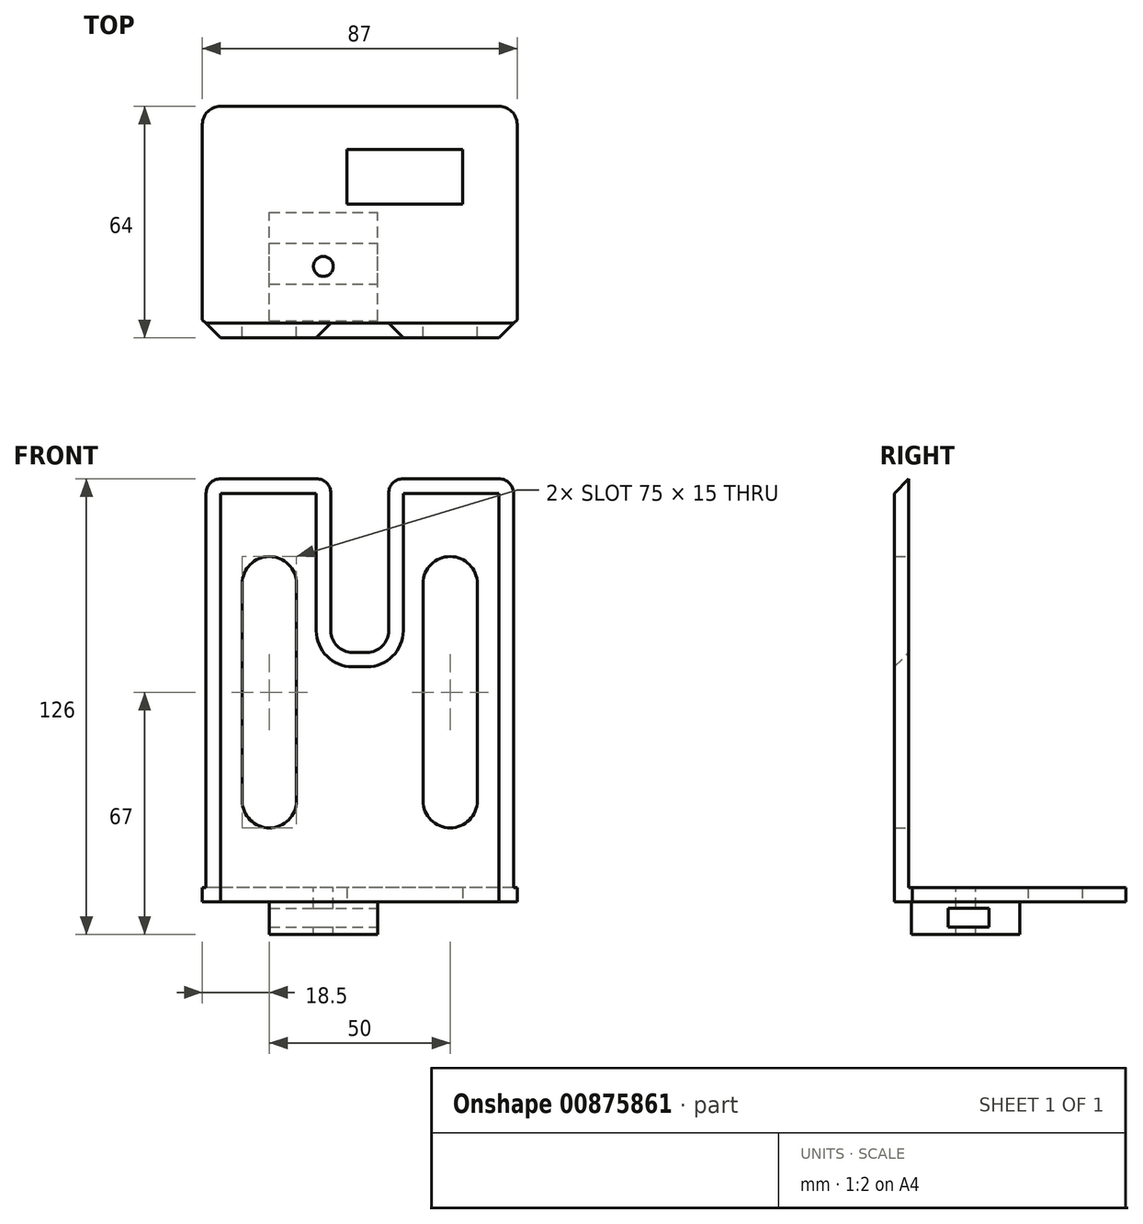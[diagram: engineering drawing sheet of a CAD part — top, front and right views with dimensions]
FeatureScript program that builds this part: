
annotation { "Feature Type Name" : "Feature", "Feature Type Description" : "" }
export const myFeature = defineFeature(function(context is Context, id is Id, definition is map)
    precondition{}
    {
        {
            var Q0;
            Q0=qCreatedBy(makeId("Front.planeOp"),FACE);
            var sketch = newSketch(context, id + "F0", { "sketchPlane" : qUnion([Q0])});
            skLineSegment(sketch, "E0.bottom", {"start": v(-43.5, 78.39) * mm, "end": v(43.5, 78.39) * mm});
            skLineSegment(sketch, "E0.top", {"start": v(-43.5, -39.61) * mm, "end": v(43.5, -39.61) * mm});
            skLineSegment(sketch, "E0.left", {"start": v(-43.5, 78.39) * mm, "end": v(-43.5, -39.61) * mm});
            skLineSegment(sketch, "E0.right", {"start": v(43.5, 78.39) * mm, "end": v(43.5, -39.61) * mm});
            skLineSegment(sketch, "E1", {"start": v(25, -11.61) * mm, "end": v(25, 48.39) * mm});
            skLineSegment(sketch, "E2.MirrorCS", {"start": v(-25, -11.61) * mm, "end": v(-25, 48.39) * mm});
            skArc(sketch, "E3.0.startCap", {"start": v(-17.5, -11.61) * mm, "mid": v(-25, -19.11) * mm, "end": v(-32.5, -11.61) * mm});
            skArc(sketch, "E3.0.endCap", {"start": v(-32.5, 48.39) * mm, "mid": v(-25, 55.89) * mm, "end": v(-17.5, 48.39) * mm});
            skLineSegment(sketch, "E3.0.left", {"start": v(-32.5, -11.61) * mm, "end": v(-32.5, 48.39) * mm});
            skLineSegment(sketch, "E3.0.right", {"start": v(-17.5, -11.61) * mm, "end": v(-17.5, 48.39) * mm});
            skLineSegment(sketch, "E4.bottom", {"start": v(-7, 78.39) * mm, "end": v(7, 78.39) * mm});
            skLineSegment(sketch, "E4.top", {"start": v(-7, 30.39) * mm, "end": v(7, 30.39) * mm});
            skLineSegment(sketch, "E4.left", {"start": v(-7, 78.39) * mm, "end": v(-7, 30.39) * mm});
            skLineSegment(sketch, "E4.right", {"start": v(7, 78.39) * mm, "end": v(7, 30.39) * mm});
            skArc(sketch, "E5.0.startCap", {"start": v(32.5, -11.61) * mm, "mid": v(25, -19.11) * mm, "end": v(17.5, -11.61) * mm});
            skArc(sketch, "E5.0.endCap", {"start": v(17.5, 48.39) * mm, "mid": v(25, 55.89) * mm, "end": v(32.5, 48.39) * mm});
            skLineSegment(sketch, "E5.0.left", {"start": v(17.5, -11.61) * mm, "end": v(17.5, 48.39) * mm});
            skLineSegment(sketch, "E5.0.right", {"start": v(32.5, -11.61) * mm, "end": v(32.5, 48.39) * mm});
            skSolve(sketch);
        }
        {
            var Q0;
            Q0=makeQuery(id+"F0.imprint","IMPRINT",FACE,{"disambiguationData":[TD([[makeQuery(id+"F0.imprint","IMPRINT",EDGE,{"derivedFrom":sQuery(id+"F0.wireOp",EDGE,"E0.top")}),1.0]])]});
            extrude(context, id + "F1", {"entities" : qUnion([Q0]), "depth" : 4 * mm, "offsetDistance" : 25 * mm});
        }
        {
            var Q0;
            Q0=makeQuery(id+"F1.opExtrude","CAP_FACE",FACE,{"disambiguationData":[OSD([sQuery(id+"F0.wireOp",EDGE,"E0.bottom"),sQuery(id+"F0.wireOp",EDGE,"E0.top"),sQuery(id+"F0.wireOp",EDGE,"E0.left"),sQuery(id+"F0.wireOp",EDGE,"E0.right"),sQuery(id+"F0.wireOp",EDGE,"E3.0.startCap"),sQuery(id+"F0.wireOp",EDGE,"E3.0.endCap"),sQuery(id+"F0.wireOp",EDGE,"E3.0.left"),sQuery(id+"F0.wireOp",EDGE,"E3.0.right"),sQuery(id+"F0.wireOp",EDGE,"E4.top"),sQuery(id+"F0.wireOp",EDGE,"E4.left"),sQuery(id+"F0.wireOp",EDGE,"E4.right"),sQuery(id+"F0.wireOp",EDGE,"E5.0.startCap"),sQuery(id+"F0.wireOp",EDGE,"E5.0.endCap"),sQuery(id+"F0.wireOp",EDGE,"E5.0.left"),sQuery(id+"F0.wireOp",EDGE,"E5.0.right")])],"isStart":true});
            var sketch = newSketch(context, id + "F2", { "sketchPlane" : qUnion([Q0])});
            skLineSegment(sketch, "E6.bottom", {"start": v(-43.5, -35.61) * mm, "end": v(43.5, -35.61) * mm});
            skLineSegment(sketch, "E6.top", {"start": v(-43.5, -39.61) * mm, "end": v(43.5, -39.61) * mm});
            skLineSegment(sketch, "E6.left", {"start": v(-43.5, -35.61) * mm, "end": v(-43.5, -39.61) * mm});
            skLineSegment(sketch, "E6.right", {"start": v(43.5, -35.61) * mm, "end": v(43.5, -39.61) * mm});
            skSolve(sketch);
        }
        {
            var Q0;
            Q0=makeQuery(id+"F2.imprint","IMPRINT",FACE,{"disambiguationData":[TD([[makeQuery(id+"F2.imprint","IMPRINT",EDGE,{"derivedFrom":sQuery(id+"F2.wireOp",EDGE,"E6.bottom")}),-1.0]])]});
            extrude(context, id + "F3", {"entities" : qUnion([Q0]), "operationType" : NewBodyOperationType.ADD, "depth" : 60 * mm, "offsetDistance" : 25 * mm});
        }
        {
            var Q0;
            Q0=makeQuery(id+"F3.boolean.opBoolean","MERGE",FACE,{"derivedFrom":[makeQuery(id+"F1.opExtrude","SWEPT_FACE",FACE,{"disambiguationData":[OSD([sQuery(id+"F0.wireOp",EDGE,"E0.top")])]}),makeQuery(id+"F3.opExtrude","SWEPT_FACE",FACE,{"disambiguationData":[OSD([sQuery(id+"F2.wireOp",EDGE,"E6.top")])]})]});
            var sketch = newSketch(context, id + "F4", { "sketchPlane" : qUnion([Q0])});
            skLineSegment(sketch, "E7.bottom", {"start": v(28.5, -33) * mm, "end": v(-3.5, -33) * mm});
            skLineSegment(sketch, "E7.top", {"start": v(28.5, -48) * mm, "end": v(-3.5, -48) * mm});
            skLineSegment(sketch, "E7.left", {"start": v(28.5, -33) * mm, "end": v(28.5, -48) * mm});
            skLineSegment(sketch, "E7.right", {"start": v(-3.5, -33) * mm, "end": v(-3.5, -48) * mm});
            skSolve(sketch);
        }
        {
            var Q0;
            Q0=makeQuery(id+"F4.imprint","IMPRINT",FACE,{"disambiguationData":[TD([[makeQuery(id+"F4.imprint","IMPRINT",EDGE,{"derivedFrom":sQuery(id+"F4.wireOp",EDGE,"E7.bottom")}),1.0]])]});
            extrude(context, id + "F5", {"entities" : qUnion([Q0]), "operationType" : NewBodyOperationType.REMOVE, "oppositeDirection" : true, "depth" : 4 * mm, "offsetDistance" : 25 * mm});
        }
        {
            var Q0;
            Q0=makeQuery(id+"F1.opExtrude","SWEPT_EDGE",EDGE,{"disambiguationData":[OSD([sQuery(id+"F0.wireOp",EDGE,"E0.bottom"),sQuery(id+"F0.wireOp",EDGE,"E0.left")])]});
            var Q1;
            Q1=makeQuery(id+"F1.opExtrude","SWEPT_EDGE",EDGE,{"disambiguationData":[OSD([sQuery(id+"F0.wireOp",EDGE,"E0.bottom"),sQuery(id+"F0.wireOp",EDGE,"E4.bottom"),sQuery(id+"F0.wireOp",EDGE,"E4.right")])]});
            var Q2;
            Q2=makeQuery(id+"F1.opExtrude","SWEPT_EDGE",EDGE,{"disambiguationData":[OSD([sQuery(id+"F0.wireOp",EDGE,"E0.bottom"),sQuery(id+"F0.wireOp",EDGE,"E4.bottom"),sQuery(id+"F0.wireOp",EDGE,"E4.left")])]});
            var Q3;
            Q3=makeQuery(id+"F1.opExtrude","SWEPT_EDGE",EDGE,{"disambiguationData":[OSD([sQuery(id+"F0.wireOp",EDGE,"E0.bottom"),sQuery(id+"F0.wireOp",EDGE,"E0.right")])]});
            var Q4;
            Q4=makeQuery(id+"F3.opExtrude","CAP_EDGE",EDGE,{"disambiguationData":[OSD([sQuery(id+"F2.wireOp",EDGE,"E6.right")])],"isStart":false});
            var Q5;
            Q5=makeQuery(id+"F3.opExtrude","CAP_EDGE",EDGE,{"disambiguationData":[OSD([sQuery(id+"F2.wireOp",EDGE,"E6.left")])],"isStart":false});
            var Q6;
            Q6=makeQuery(id+"F1.opExtrude","SWEPT_EDGE",EDGE,{"disambiguationData":[OSD([sQuery(id+"F0.wireOp",EDGE,"E4.top"),sQuery(id+"F0.wireOp",EDGE,"E4.right")])]});
            var Q7;
            Q7=makeQuery(id+"F1.opExtrude","SWEPT_EDGE",EDGE,{"disambiguationData":[OSD([sQuery(id+"F0.wireOp",EDGE,"E4.top"),sQuery(id+"F0.wireOp",EDGE,"E4.left")])]});
            fillet(context, id + "F6", {"entities" : qUnion([Q0, Q1, Q2, Q3, Q4, Q5, Q6, Q7]), "radius" : 5 * mm, "tangentPropagation" : true, "allowEdgeOverflow" : false});
        }
        {
            var Q0;
            Q0=makeQuery(id+"F3.boolean.opBoolean","MERGE",FACE,{"derivedFrom":[makeQuery(id+"F1.opExtrude","SWEPT_FACE",FACE,{"disambiguationData":[OSD([sQuery(id+"F0.wireOp",EDGE,"E0.top")])]}),makeQuery(id+"F3.opExtrude","SWEPT_FACE",FACE,{"disambiguationData":[OSD([sQuery(id+"F2.wireOp",EDGE,"E6.top")])]})]});
            var sketch = newSketch(context, id + "F7", { "sketchPlane" : qUnion([Q0])});
            skLineSegment(sketch, "E8.bottom", {"start": v(-25.06, -0.72) * mm, "end": v(4.94, -0.72) * mm});
            skLineSegment(sketch, "E8.top", {"start": v(-25.06, -30.72) * mm, "end": v(4.94, -30.72) * mm});
            skLineSegment(sketch, "E8.left", {"start": v(-25.06, -0.72) * mm, "end": v(-25.06, -30.72) * mm});
            skLineSegment(sketch, "E8.right", {"start": v(4.94, -0.72) * mm, "end": v(4.94, -30.72) * mm});
            skCircle(sketch, "E9", {"center": v(-10.06, -15.72) * mm, "radius": 2.75 * mm});
            skSolve(sketch);
        }
        {
            var Q0;
            Q0=makeQuery(id+"F7.imprint","IMPRINT",FACE,{"disambiguationData":[TD([[makeQuery(id+"F7.imprint","IMPRINT",EDGE,{"derivedFrom":sQuery(id+"F7.wireOp",EDGE,"E8.bottom")}),-1.0]])]});
            extrude(context, id + "F8", {"entities" : qUnion([Q0]), "operationType" : NewBodyOperationType.ADD, "depth" : 9 * mm, "offsetDistance" : 25 * mm});
        }
        {
            var Q0;
            Q0=makeQuery(id+"F8.boolean.opBoolean","SPLIT",FACE,{"disambiguationData":[TD([makeQuery(id+"F8.opExtrude","SWEPT_FACE",FACE,{"disambiguationData":[OSD([sQuery(id+"F7.wireOp",EDGE,"E9")])]})])],"derivedFrom":makeQuery(id+"F3.boolean.opBoolean","MERGE",FACE,{"derivedFrom":[makeQuery(id+"F1.opExtrude","SWEPT_FACE",FACE,{"disambiguationData":[OSD([sQuery(id+"F0.wireOp",EDGE,"E0.top")])]}),makeQuery(id+"F3.opExtrude","SWEPT_FACE",FACE,{"disambiguationData":[OSD([sQuery(id+"F2.wireOp",EDGE,"E6.top")])]})]})});
            extrude(context, id + "F9", {"entities" : qUnion([Q0]), "operationType" : NewBodyOperationType.REMOVE, "oppositeDirection" : true, "depth" : 5 * mm, "offsetDistance" : 25 * mm});
        }
        {
            var Q0;
            {var subQ0=sQuery(id+"F0.wireOp",EDGE,"E0.bottom");Q0=makeQuery(id+"F1.opExtrude","CAP_EDGE",EDGE,{"disambiguationData":[OSD([subQ0]),TDD([makeQuery(id+"F0.imprint","IMPRINT",EDGE,{"disambiguationData":[TD([[makeQuery(id+"F0.imprint","INTERSECT",VERTEX,{"derivedFrom":[subQ0,sQuery(id+"F0.wireOp",EDGE,"E0.left")]}),-1.0]])],"derivedFrom":subQ0})])],"isStart":false});}
            chamfer(context, id + "F10", {"entities" : qUnion([Q0]), "width" : 5 * mm, "tangentPropagation" : true});
        }
        {
            var Q0;
            Q0=makeQuery(id+"F8.opExtrude","SWEPT_FACE",FACE,{"disambiguationData":[OSD([sQuery(id+"F7.wireOp",EDGE,"E8.right")])]});
            var sketch = newSketch(context, id + "F11", { "sketchPlane" : qUnion([Q0])});
            skLineSegment(sketch, "E10.bottom", {"start": v(10.86, -41.41) * mm, "end": v(22.16, -41.41) * mm});
            skLineSegment(sketch, "E10.top", {"start": v(10.86, -46.61) * mm, "end": v(22.16, -46.61) * mm});
            skLineSegment(sketch, "E10.left", {"start": v(10.86, -41.41) * mm, "end": v(10.86, -46.61) * mm});
            skLineSegment(sketch, "E10.right", {"start": v(22.16, -41.41) * mm, "end": v(22.16, -46.61) * mm});
            skSolve(sketch);
        }
        {
            var Q0;
            Q0=makeQuery(id+"F11.imprint","IMPRINT",FACE,{"disambiguationData":[TD([[makeQuery(id+"F11.imprint","IMPRINT",EDGE,{"derivedFrom":sQuery(id+"F11.wireOp",EDGE,"E10.bottom")}),-1.0]])]});
            extrude(context, id + "F12", {"entities" : qUnion([Q0]), "operationType" : NewBodyOperationType.REMOVE, "oppositeDirection" : true, "depth" : 30.7 * mm, "offsetDistance" : 25 * mm});
        }
    });
